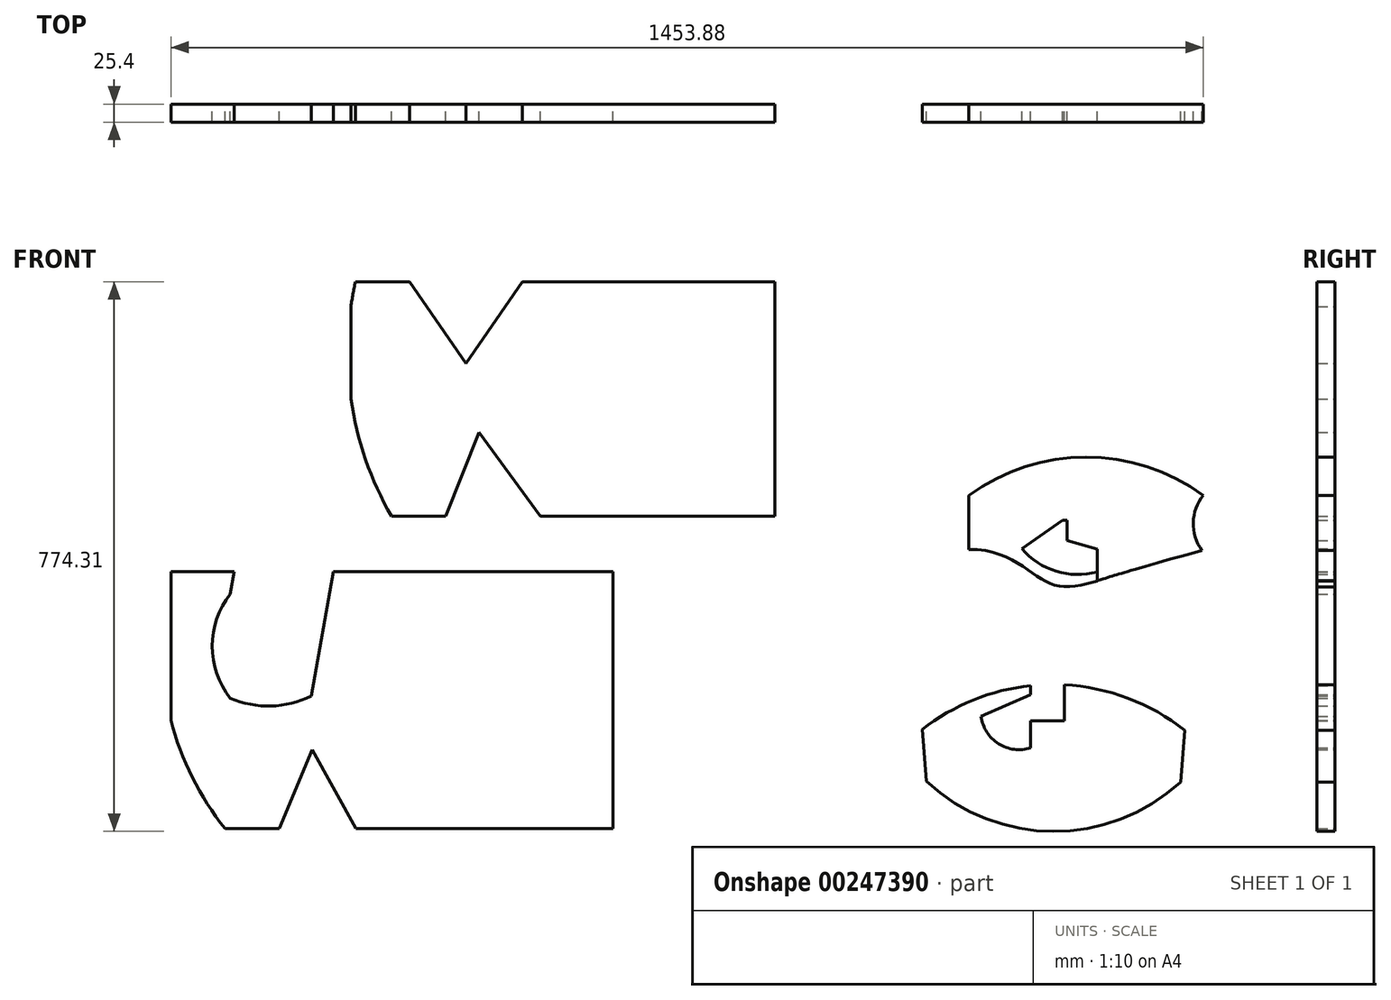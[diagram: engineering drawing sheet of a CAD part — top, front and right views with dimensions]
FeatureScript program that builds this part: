
annotation { "Feature Type Name" : "Feature", "Feature Type Description" : "" }
export const myFeature = defineFeature(function(context is Context, id is Id, definition is map)
    precondition{}
    {
        {
            var Q0;
            Q0=qCreatedBy(makeId("Front.planeOp"),FACE);
            var sketch = newSketch(context, id + "F0", { "sketchPlane" : qUnion([Q0])});
            skLineSegment(sketch, "E0.bottom", {"start": v(-309.4, 282.25) * mm, "end": v(287.5, 282.25) * mm});
            skLineSegment(sketch, "E0.top", {"start": v(-309.4, -47.95) * mm, "end": v(287.5, -47.95) * mm});
            skLineSegment(sketch, "E0.left", {"start": v(-309.4, 282.25) * mm, "end": v(-309.4, -47.95) * mm});
            skLineSegment(sketch, "E0.right", {"start": v(287.5, 282.25) * mm, "end": v(287.5, -47.95) * mm});
            skLineSegment(sketch, "E1", {"start": v(-68.1, 282.25) * mm, "end": v(-147.48, 167.29) * mm});
            skLineSegment(sketch, "E2", {"start": v(-147.48, 167.29) * mm, "end": v(-226.86, 282.25) * mm});
            skLineSegment(sketch, "E3", {"start": v(-176.06, -47.95) * mm, "end": v(-128.89, 69.96) * mm});
            skLineSegment(sketch, "E4", {"start": v(-128.89, 69.96) * mm, "end": v(-42.7, -47.95) * mm});
            skPoint(sketch, "E5.first.point", {"position": v(-303.06, 282.25) * mm});
            skPoint(sketch, "E5.second.point", {"position": v(-252.26, -47.95) * mm});
            skPoint(sketch, "E5.third.point", {"position": v(-309.4, 117.15) * mm});
            skArc(sketch, "E6", {"start": v(-303.06, 282.25) * mm, "mid": v(-308.7, 112.37) * mm, "end": v(-252.26, -47.95) * mm});
            skSolve(sketch);
        }
        {
            var Q0;
            {var subQ2=sQuery(id+"F0.wireOp",EDGE,"E0.right");Q0=makeQuery(id+"F0.imprint","IMPRINT",FACE,{"disambiguationData":[TD([[makeQuery(id+"F0.imprint","IMPRINT",EDGE,{"derivedFrom":subQ2}),-1.0]])]});}
            var Q1;
            {var subQ0=sQuery(id+"F0.wireOp",EDGE,"E6");var subQ1=sQuery(id+"F0.wireOp",EDGE,"E0.left");var subQ2=makeQuery(id+"F0.imprint","INTERSECT",VERTEX,{"disambiguationData":[OD(0.0)],"derivedFrom":[subQ1,subQ0]});Q1=makeQuery(id+"F0.imprint","IMPRINT",FACE,{"disambiguationData":[TD([[makeQuery(id+"F0.imprint","IMPRINT",EDGE,{"disambiguationData":[TD([[subQ2,-1.0]])],"derivedFrom":subQ1}),-1.0]])]});}
            extrude(context, id + "F1", {"entities" : qUnion([Q0, Q1]), "depth" : 25.4 * mm});
        }
        {
            var Q0;
            Q0=qCreatedBy(makeId("Front.planeOp"),FACE);
            var sketch = newSketch(context, id + "F2", { "sketchPlane" : qUnion([Q0])});
            skLineSegment(sketch, "E7.bottom", {"start": v(-562.93, -126.23) * mm, "end": v(59.37, -126.23) * mm});
            skLineSegment(sketch, "E7.top", {"start": v(-562.93, -488.18) * mm, "end": v(59.37, -488.18) * mm});
            skLineSegment(sketch, "E7.left", {"start": v(-562.93, -126.23) * mm, "end": v(-562.93, -488.18) * mm});
            skLineSegment(sketch, "E7.right", {"start": v(59.37, -126.23) * mm, "end": v(59.37, -488.18) * mm});
            skLineSegment(sketch, "E8", {"start": v(-410.53, -488.18) * mm, "end": v(-363.84, -376.94) * mm});
            skLineSegment(sketch, "E9", {"start": v(-363.84, -376.94) * mm, "end": v(-302.58, -488.18) * mm});
            skArc(sketch, "E10", {"start": v(-562.93, -126.23) * mm, "mid": v(-567.5, -316.2) * mm, "end": v(-486.73, -488.18) * mm});
            skLineSegment(sketch, "E11", {"start": v(-474.03, -126.23) * mm, "end": v(-479.54, -157.5) * mm});
            skLineSegment(sketch, "E12", {"start": v(-334.33, -126.23) * mm, "end": v(-365.2, -301.33) * mm});
            skLineSegment(sketch, "E13", {"start": v(-479.54, -157.5) * mm, "end": v(-479.54, -304.32) * mm});
            skLineSegment(sketch, "E14", {"start": v(-479.54, -304.32) * mm, "end": v(-365.2, -301.33) * mm});
            skArc(sketch, "E15", {"start": v(-479.54, -157.5) * mm, "mid": v(-504.86, -230.91) * mm, "end": v(-479.54, -304.32) * mm});
            skArc(sketch, "E16", {"start": v(-479.54, -304.32) * mm, "mid": v(-422.04, -315.4) * mm, "end": v(-365.2, -301.33) * mm});
            skSolve(sketch);
        }
        {
            var Q0;
            {var subQ1=sQuery(id+"F2.wireOp",EDGE,"E7.right");Q0=makeQuery(id+"F2.imprint","IMPRINT",FACE,{"disambiguationData":[TD([[makeQuery(id+"F2.imprint","IMPRINT",EDGE,{"derivedFrom":subQ1}),-1.0]])]});}
            extrude(context, id + "F3", {"entities" : qUnion([Q0]), "depth" : 25.4 * mm});
        }
        {
            var Q0;
            Q0=qCreatedBy(makeId("Front.planeOp"),FACE);
            var sketch = newSketch(context, id + "F4", { "sketchPlane" : qUnion([Q0])});
            skLineSegment(sketch, "E17.bottom", {"start": v(560.75, -18.47) * mm, "end": v(890.95, -18.47) * mm});
            skLineSegment(sketch, "E17.left", {"start": v(560.75, -18.47) * mm, "end": v(560.75, -94.67) * mm});
            skPoint(sketch, "E18.third.point", {"position": v(725.85, 35.21) * mm});
            skArc(sketch, "E19", {"start": v(890.95, -18.47) * mm, "mid": v(876.75, -56.99) * mm, "end": v(889.07, -96.14) * mm});
            skArc(sketch, "E20", {"start": v(890.95, -18.47) * mm, "mid": v(725.85, 35.21) * mm, "end": v(560.75, -18.47) * mm});
            skFitSpline(sketch, "E21", {"points": [v(560.75, -94.67) * mm, v(648.47, -126.73) * mm, v(694.1, -147.22) * mm, v(751.74, -135.8) * mm, v(889.07, -96.14) * mm], "startDerivative": vector(455.77, 10.11) * mm, "endDerivative": vector(1007, 281.43) * mm});
            skLineSegment(sketch, "E22", {"start": v(741.72, -94.54) * mm, "end": v(741.72, -139) * mm});
            skLineSegment(sketch, "E23", {"start": v(699, -82.29) * mm, "end": v(741.72, -94.54) * mm});
            skLineSegment(sketch, "E24", {"start": v(699, -82.29) * mm, "end": v(699, -53.71) * mm});
            skLineSegment(sketch, "E25", {"start": v(699, -53.71) * mm, "end": v(692.64, -53.71) * mm});
            skLineSegment(sketch, "E26", {"start": v(692.64, -53.71) * mm, "end": v(635.43, -93.78) * mm});
            skLineSegment(sketch, "E27", {"start": v(741.72, -139) * mm, "end": v(741.72, -126.3) * mm});
            skArc(sketch, "E28", {"start": v(635.43, -93.78) * mm, "mid": v(683.81, -125.6) * mm, "end": v(741.72, -126.3) * mm});
            skPoint(sketch, "E29", {"position": v(677.68, -143.64) * mm});
            skPoint(sketch, "E30", {"position": v(683.81, -125.6) * mm});
            skLineSegment(sketch, "E31", {"start": v(741.34, -126.4) * mm, "end": v(741.34, -139.1) * mm});
            skSolve(sketch);
        }
        {
            var Q0;
            Q0=makeQuery(id+"F4.imprint","IMPRINT",FACE,{"disambiguationData":[TD([[makeQuery(id+"F4.imprint","IMPRINT",EDGE,{"derivedFrom":sQuery(id+"F4.wireOp",EDGE,"E17.bottom")}),1.0]])]});
            var Q1;
            Q1=makeQuery(id+"F4.imprint","IMPRINT",FACE,{"disambiguationData":[TD([[makeQuery(id+"F4.imprint","IMPRINT",EDGE,{"derivedFrom":sQuery(id+"F4.wireOp",EDGE,"E17.bottom")}),-1.0]])]});
            extrude(context, id + "F5", {"entities" : qUnion([Q0, Q1]), "depth" : 25.4 * mm});
        }
        {
            var Q0;
            Q0=qCreatedBy(makeId("Front.planeOp"),FACE);
            var sketch = newSketch(context, id + "F6", { "sketchPlane" : qUnion([Q0])});
            skLineSegment(sketch, "E32", {"start": v(495, -348.53) * mm, "end": v(500.82, -421.32) * mm});
            skLineSegment(sketch, "E33", {"start": v(858.8, -422.35) * mm, "end": v(864.6, -349.56) * mm});
            skPoint(sketch, "E34", {"position": v(679.15, -348.53) * mm});
            skPoint(sketch, "E35", {"position": v(680.36, -428.56) * mm});
            skArc(sketch, "E36", {"start": v(864.6, -349.56) * mm, "mid": v(679.98, -285.03) * mm, "end": v(495, -348.53) * mm});
            skArc(sketch, "E37", {"start": v(500.82, -421.32) * mm, "mid": v(679.6, -492.06) * mm, "end": v(858.8, -422.35) * mm});
            skPoint(sketch, "E38", {"position": v(695.36, -285.47) * mm});
            skLineSegment(sketch, "E39", {"start": v(695.36, -285.47) * mm, "end": v(695.36, -336.27) * mm});
            skLineSegment(sketch, "E40", {"start": v(695.36, -336.27) * mm, "end": v(647.74, -336.27) * mm});
            skLineSegment(sketch, "E41", {"start": v(647.74, -336.27) * mm, "end": v(647.74, -374.37) * mm});
            skLineSegment(sketch, "E42", {"start": v(647.74, -286.69) * mm, "end": v(647.74, -299.39) * mm});
            skLineSegment(sketch, "E43", {"start": v(647.74, -299.39) * mm, "end": v(577.96, -330) * mm});
            skArc(sketch, "E44", {"start": v(577.96, -330) * mm, "mid": v(602.5, -368.44) * mm, "end": v(647.74, -374.37) * mm});
            skSolve(sketch);
        }
        {
            var Q0;
            {var subQ2=sQuery(id+"F6.wireOp",EDGE,"E32");Q0=makeQuery(id+"F6.imprint","IMPRINT",FACE,{"disambiguationData":[TD([[makeQuery(id+"F6.imprint","IMPRINT",EDGE,{"derivedFrom":subQ2}),1.0]])]});}
            extrude(context, id + "F7", {"entities" : qUnion([Q0]), "depth" : 25.4 * mm});
        }
    });
